# Revit family: Ленточный двухскатный зенитный фонарь M8CITY_Д_ВЕНТ-створки_2017
name_source: partatom
category: Оборудование
revit_build: Autodesk Revit 2017 (Build: 20170118_1100(x64)
units: mm (PartAtom-declared; Revit-internal decimal feet)

## family parameters
Всегда вертикально = Нет
Общий = Нет
Основа = Крыша
При загрузке вырезать с полостями = Нет
Размер круглого соединителя = Использовать диаметр
Тип детали = Нормальный
Точка расчета площади = Нет

## types (1)
- Зенитный фонарь M8CITY Л-Д-ВЕНТ-створки
    ADSK_Завод-изготовитель = ООО ''Завод М8 Сити''
    ADSK_Код изделия = ТУ BY 191302027.002-2013
    ADSK_Количество = 1
    ADSK_Обозначение = M8CITY
    ADSK_Размер_Высота = 500 мм
    ADSK_Размер_Длина = 10000 мм
    ADSK_Размер_Ширина = 3200 мм
    N растров = 10
    N ферм = 9
    Table 1 = Описание
    Table 2 = Маркировка
    URL = www.m8city.by
    Вид створки = 1
    Видимость створки двойной = Нет
    Высота = 573 мм
    Высота основания = 500 мм
    Длина = 10000 мм
    Длина проёма = 10000 мм
    Длина проёма ввод = 10000 мм
    Длина створки = 1000 мм
    Длина створки ном = 1000 мм
    Заполнение = 1
    Количество створок = 3
    Количество створок ном = 3
    Количество типовых растров = 9
    Количество ферм = 5
    Крайний растр = 805 мм
    Смещение массива = 1865 мм
    Типовой растр = 1060 мм
    Угол наклона к горизонту = 30.00°
    Угол наклона к горизонту ном = 30.00°
    Шаг массива = 3180 мм
    Шаг типовой = 1060 мм
    Ширина = 3200 мм
    Ширина проёма = 3200 мм
    Ширина проёма ввод = 3200 мм
